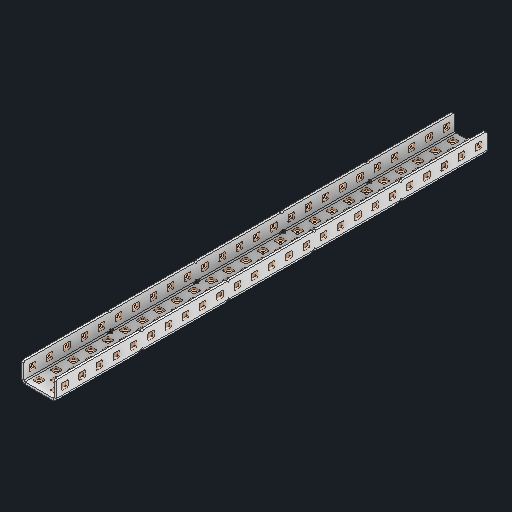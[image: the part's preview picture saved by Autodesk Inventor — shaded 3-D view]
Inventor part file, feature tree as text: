
AUTODESK INVENTOR PART (.ipt)
format: ipt  version: 2024 (Build 280153000, 153)  size: 1,563,648 bytes
history: native  units: in
note: dims shown in document units (in); Inventor stores cm internally (conversion verified against a paired STEP export)
features: other x132, extrude x123, sheet_metal_op x11, pattern_linear x2, mirror x1, chamfer x1, sketch x1
ambient origin geometry x8: Origin, YZ Plane, XZ Plane, XY Plane, X Axis, Y Axis, Z Axis, Center Point
bodies: Solid1 (feature_tree), Body (feature_tree)
feature tree (271):
  sheet_metal_op  "Flanges"
  other  "Flange Pattern Plane"
  other  "Flange Pattern Sketch"
  sheet_metal_op  "Flange Pattern"
  sheet_metal_op  "Body Pattern"
  pattern_linear  "Center Pattern"  Spacing1=12.5in  [1 undecoded]
  other  "Arc Length"
  mirror  "Notch Mirror"
  pattern_linear  "Notch Pattern"  Spacing1=0.0625in  [1 undecoded]
  chamfer  "End Chamfer"
  extrude  "Half Cut"  Depth=0.0625in
  other  "Plate1"
  sketch  "Sketch2"  dims[d0=1.0in d1=12.5in d2=0.0625in d3=0.0625in d4=0.0312in d5=0.125in d6=0.0625in d7=0.5in d8=90.0deg d9=0.0312in d10=0.25in d11=0.0625in d12=0.0625in d16=0.182in d17=0.02in d18=0.0625in d19=0.0in d20=0.25in d21=0.25in d38=9.8425in d40=0.5in d41=0.7874in d43=1.0in d46=0.172in d47=1.0in d48=0.0in d49=0.182in d50=0.02in d51=0.25in d52=0.25in d53=0.0625in d54=0.0in d55=0.172in d56=1.0in d57=0.0in d58=0.25in d60=9.8425in d62=0.5in d63=0.7874in d65=0.5in d85=0.1473in d86=0.1782in d88=0.04in d89=0.0625in d90=0.0in d91=0.04in d92=0.0491in d95=2.5in d96=0.04in d97=0.25in d98=45.0deg d99=0.25in d100=0.5in d101=0.0in d102=2.497in d106=0.182in d107=0.02in d108=0.5in d109=0.5in d110=0.0625in d111=0.0in d112=0.172in d113=0.5in d114=0.0in d117=0.5in d118=0.5in d119=0.5in]
  other  "Plate2"
  sheet_metal_op  "Bend1"
  sheet_metal_op  "Corner1"
  other  "Srf1"
  other  "Srf2"
  other  "Srf91"
  sheet_metal_op  "Body Pattern Sketch"
  other  "Srf92"
  other  "Srf786"
  other  "Srf823"
  other  "Srf824"
  other  "Srf825"
  other  "Srf826"
  other  "Srf827"
  other  "Srf828"
  other  "Srf829"
  other  "Srf856"
  other  "Srf857"
  other  "Srf858"
  other  "Srf859"
  other  "Srf860"
  other  "Srf861"
  other  "Srf862"
  other  "Srf889"
  other  "Srf890"
  other  "Srf891"
  other  "Srf892"
  other  "Srf893"
  other  "Srf894"
  other  "Srf895"
  other  "Srf896"
  other  "Srf922"
  other  "Srf923"
  other  "Srf924"
  other  "Srf925"
  other  "Srf926"
  other  "Srf959"
  other  "Srf960"
  other  "Srf961"
  other  "Srf962"
  other  "Srf963"
  other  "Srf996"
  other  "Srf997"
  other  "Srf998"
  other  "Srf999"
  other  "Srf1000"
  other  "Srf1143"
  other  "Srf1144"
  other  "Srf1145"
  other  "Srf1146"
  other  "Srf1147"
  other  "Srf1148"
  other  "Srf1149"
  other  "Srf1150"
  other  "Srf1151"
  other  "Srf1152"
  other  "Srf1153"
  other  "Srf1154"
  other  "Srf1155"
  other  "Srf1156"
  other  "Srf1157"
  other  "Srf1158"
  other  "Srf1159"
  other  "Srf1160"
  other  "Srf1161"
  other  "Srf1162"
  other  "Srf1163"
  other  "Srf1164"
  other  "Srf1165"
  other  "Srf1166"
  other  "Srf1167"
  other  "Srf1168"
  other  "Srf1169"
  other  "Srf1170"
  other  "Srf1171"
  other  "Srf1172"
  other  "Srf1173"
  other  "Srf1174"
  other  "Srf1175"
  other  "Srf1176"
  other  "Srf1177"
  other  "Srf1178"
  other  "Srf1199"
  other  "Srf1200"
  other  "Srf1201"
  other  "Srf1202"
  other  "Srf1203"
  other  "Srf1204"
  other  "Srf1205"
  other  "Srf1206"
  other  "Srf1207"
  other  "Srf1208"
  other  "Srf1209"
  other  "Srf1210"
  other  "Srf1211"
  other  "Srf1212"
  other  "Srf1213"
  other  "Srf1214"
  other  "Srf1215"
  other  "Srf1216"
  other  "Srf1217"
  other  "Srf1218"
  other  "Srf1219"
  other  "Srf1220"
  other  "Srf1221"
  other  "Srf1222"
  other  "Srf1223"
  other  "Srf1224"
  other  "Srf1225"
  other  "Srf1226"
  other  "Srf1227"
  other  "Srf1228"
  other  "Srf1229"
  other  "Srf1230"
  other  "Srf1231"
  other  "Srf1232"
  other  "Srf1233"
  other  "Srf1234"
  other  "Srf1255"
  other  "Srf1256"
  other  "Srf1257"
  other  "Srf1258"
  other  "Srf1259"
  other  "Srf1260"
  other  "Srf1261"
  other  "Srf1262"
  other  "Srf1263"
  other  "Srf1264"
  other  "Srf1265"
  sheet_metal_op  "Flange Stamp"
  sheet_metal_op  "Flange Circle"
  sheet_metal_op  "Body Stamp"
  sheet_metal_op  "Body Circle"
  other  "Center Stamp"
  other  "Center Circle"
  sheet_metal_op  "Notch"
  extrude  "ExtrusionSrf2"  Depth=0.0312in
  extrude  "ExtrusionSrf92"  Depth=0.5in
  extrude  "ExtrusionSrf823"  Depth=0.0625in
  extrude  "ExtrusionSrf824"  Depth=0.5in TaperAngle=90.0deg
  extrude  "ExtrusionSrf825"  Depth=0.5in
  extrude  "ExtrusionSrf826"  Depth=0.0625in
  extrude  "ExtrusionSrf827"  Depth=0.0625in
  extrude  "ExtrusionSrf828"  Depth=0.5in
  extrude  "ExtrusionSrf829"  Depth=0.02in
  extrude  "ExtrusionSrf856"  Depth=0.0625in
  extrude  "ExtrusionSrf857"  TaperAngle=0.0deg  [1 undecoded]
  extrude  "ExtrusionSrf858"  Depth=0.5in
  extrude  "ExtrusionSrf859"  Depth=0.5in
  extrude  "ExtrusionSrf860"  Depth=0.5in
  extrude  "ExtrusionSrf861"  Depth=0.5in
  extrude  "ExtrusionSrf862"  Depth=1.0in TaperAngle=0.0deg
  extrude  "ExtrusionSrf889"  Depth=0.5in
  extrude  "ExtrusionSrf890"  Depth=0.02in
  extrude  "ExtrusionSrf891"  Depth=0.5in
  extrude  "ExtrusionSrf892"  Depth=0.5in
  extrude  "ExtrusionSrf893"  Depth=0.0625in
  extrude  "ExtrusionSrf894"  TaperAngle=0.0deg  [1 undecoded]
  extrude  "ExtrusionSrf895"  Depth=0.5in
  extrude  "ExtrusionSrf896"  Depth=1.0in TaperAngle=0.0deg
  extrude  "ExtrusionSrf922"  Depth=0.5in
  extrude  "ExtrusionSrf923"  Depth=0.5in
  extrude  "ExtrusionSrf924"  Depth=0.5in
  extrude  "ExtrusionSrf925"  Depth=0.5in
  extrude  "ExtrusionSrf926"  Depth=0.5in
  extrude  "ExtrusionSrf959"  Depth=0.5in
  extrude  "ExtrusionSrf960"  Depth=0.0625in
  extrude  "ExtrusionSrf961"  TaperAngle=0.0deg  [1 undecoded]
  extrude  "ExtrusionSrf962"  Depth=0.5in
  extrude  "ExtrusionSrf963"  Depth=0.5in
  extrude  "ExtrusionSrf996"  Depth=2.5in
  extrude  "ExtrusionSrf997"  Depth=0.5in TaperAngle=45.0deg
  extrude  "ExtrusionSrf998"  Depth=0.5in
  extrude  "ExtrusionSrf999"  Depth=0.5in TaperAngle=0.0deg
  extrude  "ExtrusionSrf1000"  Depth=0.5in
  extrude  "ExtrusionSrf1143"  Depth=0.5in
  extrude  "ExtrusionSrf1144"  Depth=0.02in
  extrude  "ExtrusionSrf1145"  Depth=0.5in
  extrude  "ExtrusionSrf1146"  Depth=0.5in
  extrude  "ExtrusionSrf1147"  Depth=0.0625in
  extrude  "ExtrusionSrf1148"  TaperAngle=0.0deg  [1 undecoded]
  extrude  "ExtrusionSrf1149"  Depth=0.5in
  extrude  "ExtrusionSrf1150"  Depth=0.5in TaperAngle=0.0deg
  extrude  "ExtrusionSrf1151"  Depth=0.5in
  extrude  "ExtrusionSrf1152"  Depth=0.5in
  extrude  "ExtrusionSrf1153"  Depth=0.5in
  extrude  "ExtrusionSrf1154"  [1 undecoded]
  extrude  "ExtrusionSrf1155"  [1 undecoded]
  extrude  "ExtrusionSrf1156"  [1 undecoded]
  extrude  "ExtrusionSrf1157"  [1 undecoded]
  extrude  "ExtrusionSrf1158"  [1 undecoded]
  extrude  "ExtrusionSrf1159"  [1 undecoded]
  extrude  "ExtrusionSrf1160"  [1 undecoded]
  extrude  "ExtrusionSrf1161"  [1 undecoded]
  extrude  "ExtrusionSrf1162"  [1 undecoded]
  extrude  "ExtrusionSrf1163"  [1 undecoded]
  extrude  "ExtrusionSrf1164"  [1 undecoded]
  extrude  "ExtrusionSrf1165"  [1 undecoded]
  extrude  "ExtrusionSrf1166"  [1 undecoded]
  extrude  "ExtrusionSrf1167"  [1 undecoded]
  extrude  "ExtrusionSrf1168"  [1 undecoded]
  extrude  "ExtrusionSrf1169"  [1 undecoded]
  extrude  "ExtrusionSrf1170"  [1 undecoded]
  extrude  "ExtrusionSrf1171"  [1 undecoded]
  extrude  "ExtrusionSrf1172"  [1 undecoded]
  extrude  "ExtrusionSrf1173"  [1 undecoded]
  extrude  "ExtrusionSrf1174"  [1 undecoded]
  extrude  "ExtrusionSrf1175"  [1 undecoded]
  extrude  "ExtrusionSrf1176"  [1 undecoded]
  extrude  "ExtrusionSrf1177"  [1 undecoded]
  extrude  "ExtrusionSrf1178"  [1 undecoded]
  extrude  "ExtrusionSrf1199"  [1 undecoded]
  extrude  "ExtrusionSrf1200"  [1 undecoded]
  extrude  "ExtrusionSrf1201"  [1 undecoded]
  extrude  "ExtrusionSrf1202"  [1 undecoded]
  extrude  "ExtrusionSrf1203"  [1 undecoded]
  extrude  "ExtrusionSrf1204"  [1 undecoded]
  extrude  "ExtrusionSrf1205"  [1 undecoded]
  extrude  "ExtrusionSrf1206"  [1 undecoded]
  extrude  "ExtrusionSrf1207"  [1 undecoded]
  extrude  "ExtrusionSrf1208"  [1 undecoded]
  extrude  "ExtrusionSrf1209"  [1 undecoded]
  extrude  "ExtrusionSrf1210"  [1 undecoded]
  extrude  "ExtrusionSrf1211"  [1 undecoded]
  extrude  "ExtrusionSrf1212"  [1 undecoded]
  extrude  "ExtrusionSrf1213"  [1 undecoded]
  extrude  "ExtrusionSrf1214"  [1 undecoded]
  extrude  "ExtrusionSrf1215"  [1 undecoded]
  extrude  "ExtrusionSrf1216"  [1 undecoded]
  extrude  "ExtrusionSrf1217"  [1 undecoded]
  extrude  "ExtrusionSrf1218"  [1 undecoded]
  extrude  "ExtrusionSrf1219"  [1 undecoded]
  extrude  "ExtrusionSrf1220"  [1 undecoded]
  extrude  "ExtrusionSrf1221"  [1 undecoded]
  extrude  "ExtrusionSrf1222"  [1 undecoded]
  extrude  "ExtrusionSrf1223"  [1 undecoded]
  extrude  "ExtrusionSrf1224"  [1 undecoded]
  extrude  "ExtrusionSrf1225"  [1 undecoded]
  extrude  "ExtrusionSrf1226"  [1 undecoded]
  extrude  "ExtrusionSrf1227"  [1 undecoded]
  extrude  "ExtrusionSrf1228"  [1 undecoded]
  extrude  "ExtrusionSrf1229"  [1 undecoded]
  extrude  "ExtrusionSrf1230"  [1 undecoded]
  extrude  "ExtrusionSrf1231"  [1 undecoded]
  extrude  "ExtrusionSrf1232"  [1 undecoded]
  extrude  "ExtrusionSrf1233"  [1 undecoded]
  extrude  "ExtrusionSrf1234"  [1 undecoded]
  extrude  "ExtrusionSrf1255"  [1 undecoded]
  extrude  "ExtrusionSrf1256"  [1 undecoded]
  extrude  "ExtrusionSrf1257"  [1 undecoded]
  extrude  "ExtrusionSrf1258"  [1 undecoded]
  extrude  "ExtrusionSrf1259"  [1 undecoded]
  extrude  "ExtrusionSrf1260"  [1 undecoded]
  extrude  "ExtrusionSrf1261"  [1 undecoded]
  extrude  "ExtrusionSrf1262"  [1 undecoded]
  extrude  "ExtrusionSrf1263"  [1 undecoded]
  extrude  "ExtrusionSrf1264"  [1 undecoded]
  extrude  "ExtrusionSrf1265"  [1 undecoded]
note: 78 required parameter values undecoded (feature->parameter linkage not recoverable at this tier; creation-order binding heuristic only, values carry confidence <= 0.55)
